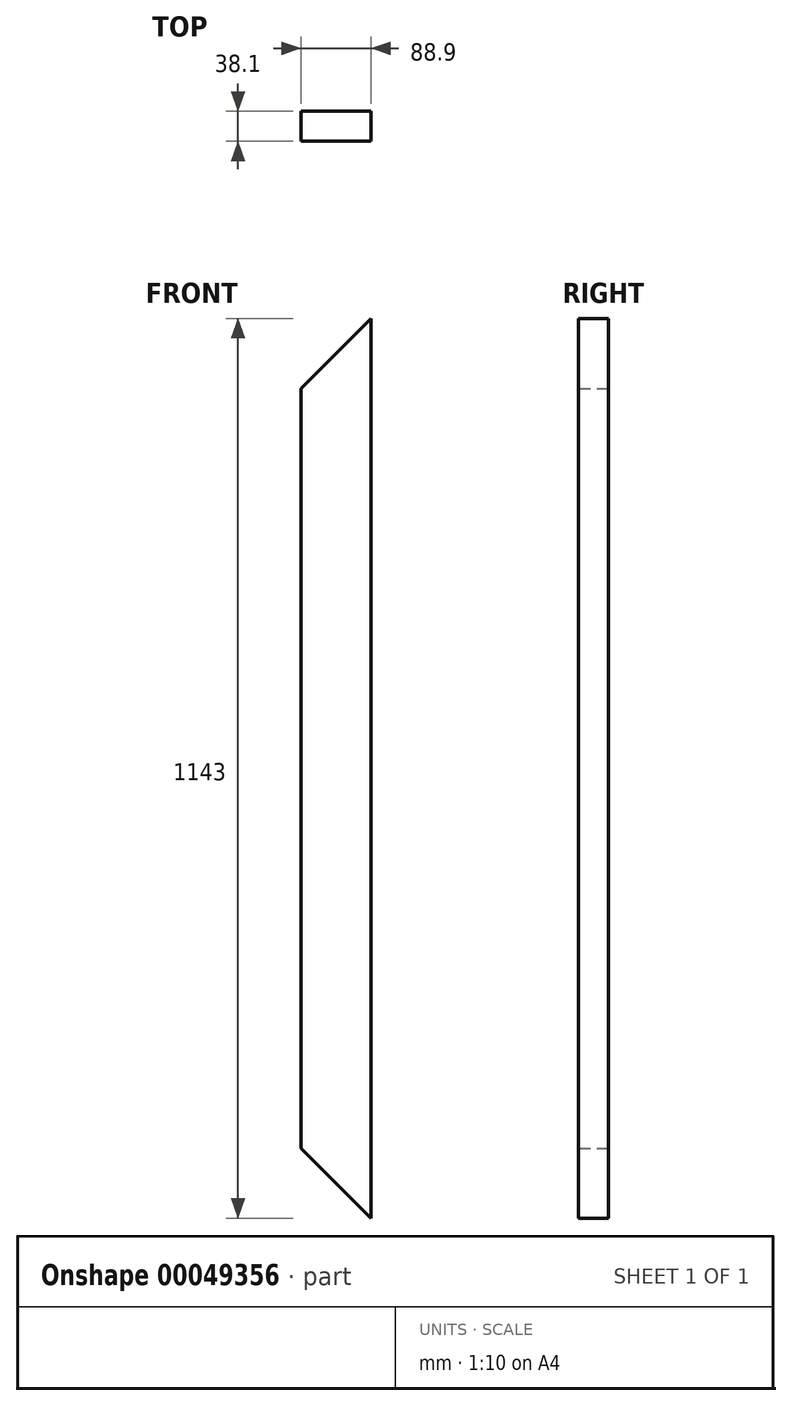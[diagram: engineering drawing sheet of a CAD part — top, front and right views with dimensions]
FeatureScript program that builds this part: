
annotation { "Feature Type Name" : "Feature", "Feature Type Description" : "" }
export const myFeature = defineFeature(function(context is Context, id is Id, definition is map)
    precondition{}
    {
        {
            var Q0;
            Q0=qCreatedBy(makeId("Top.planeOp"),FACE);
            var sketch = newSketch(context, id + "F0", { "sketchPlane" : qUnion([Q0])});
            skLineSegment(sketch, "E0.rect.bottom", {"start": v(44.45, -19.05) * mm, "end": v(-44.45, -19.05) * mm});
            skLineSegment(sketch, "E0.rect.top", {"start": v(44.45, 19.05) * mm, "end": v(-44.45, 19.05) * mm});
            skLineSegment(sketch, "E0.rect.left", {"start": v(44.45, -19.05) * mm, "end": v(44.45, 19.05) * mm});
            skLineSegment(sketch, "E0.rect.right", {"start": v(-44.45, -19.05) * mm, "end": v(-44.45, 19.05) * mm});
            skPoint(sketch, "E0.rect.middle", {"position": v(0, 0) * mm});
            skSolve(sketch);
        }
        {
            var Q0;
            Q0 = qSketchRegion(id + "F0", true);
            extrude(context, id + "F1", {"entities" : qUnion([Q0]), "endBound" : BoundingType.SYMMETRIC, "depth" : 1143 * mm});
        }
        {
            var Q0;
            Q0=makeQuery(id+"F1.opExtrude","SWEPT_FACE",FACE,{"disambiguationData":[OSD([sQuery(id+"F0.wireOp",EDGE,"E0.rect.top")])]});
            var sketch = newSketch(context, id + "F2", { "sketchPlane" : qUnion([Q0])});
            skLineSegment(sketch, "E1", {"start": v(-44.45, 571.5) * mm, "end": v(44.45, 482.6) * mm});
            skLineSegment(sketch, "E2", {"start": v(44.45, 482.6) * mm, "end": v(44.45, 571.5) * mm});
            skLineSegment(sketch, "E3", {"start": v(44.45, 571.5) * mm, "end": v(-44.45, 571.5) * mm});
            skLineSegment(sketch, "E4.MirrorCS", {"start": v(-44.45, -571.5) * mm, "end": v(44.45, -482.6) * mm});
            skLineSegment(sketch, "E5.MirrorCS", {"start": v(44.45, -482.6) * mm, "end": v(44.45, -571.5) * mm});
            skLineSegment(sketch, "E6.MirrorCS", {"start": v(44.45, -571.5) * mm, "end": v(-44.45, -571.5) * mm});
            skSolve(sketch);
        }
        {
            var Q0;
            Q0=makeQuery(id+"F2.imprint","IMPRINT",FACE,{"disambiguationData":[TD([[makeQuery(id+"F2.imprint","IMPRINT",EDGE,{"derivedFrom":sQuery(id+"F2.wireOp",EDGE,"E1")}),1.0]])]});
            var Q1;
            Q1=makeQuery(id+"F2.imprint","IMPRINT",FACE,{"disambiguationData":[TD([[makeQuery(id+"F2.imprint","IMPRINT",EDGE,{"derivedFrom":sQuery(id+"F2.wireOp",EDGE,"E4.MirrorCS")}),-1.0]])]});
            extrude(context, id + "F3", {"entities" : qUnion([Q0, Q1]), "operationType" : NewBodyOperationType.REMOVE, "endBound" : BoundingType.THROUGH_ALL, "oppositeDirection" : true, "depth" : 25.4 * mm});
        }
    });
